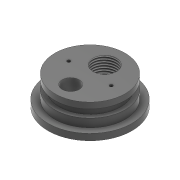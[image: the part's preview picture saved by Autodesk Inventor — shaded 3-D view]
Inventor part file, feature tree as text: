
AUTODESK INVENTOR PART (.ipt)
format: ipt  version: 2022.3 (Build 263350000, 350)  size: 176,640 bytes
history: native  units: mm
features: extrude x8, sketch x8, other x1, plane x1, thread x1
ambient origin geometry x8: Origin, YZ Plane, XZ Plane, XY Plane, X Axis, Y Axis, Z Axis, Center Point
bodies: Body1 (feature_tree)
feature tree (19):
  other  "Sólido1"
  extrude  "Extrusión1"  Depth=4.0mm TaperAngle=0.0deg
  extrude  "Extrusión2"  Depth=13.8mm TaperAngle=0.0deg
  plane  "Plano de trabajo1"
  extrude  "Extrusión6"  Depth=37.85mm
  extrude  "Extrusión7"  Depth=5.0mm
  extrude  "Extrusión8"  Depth=17.05mm
  extrude  "Extrusión9"  Depth=4.45mm
  extrude  "Extrusión10"  Depth=1.0mm
  thread  "Rosca2"  [1 undecoded]
  extrude  "Extrusión11"  Depth=5.0mm
  sketch  "Boceto1"  dims[d0=52.0mm d1=4.0mm d2=0.0mm]
  sketch  "Boceto2"  dims[d3=43.55mm d4=13.8mm d5=0.0mm]
  sketch  "Boceto6"  dims[d17=-3.6mm d18=37.85mm]
  sketch  "Boceto7"  dims[d19=5.0mm d20=0.0mm d21=5.5mm]
  sketch  "Boceto8"  dims[d22=17.05mm d23=19.15mm]
  sketch  "Boceto9"  dims[d24=4.45mm d25=0.0mm d26=10.55mm]
  sketch  "Boceto10"  dims[d27=15.0mm d28=0.0mm d29=1.0mm d30=23.25mm]
  sketch  "Boceto11"  dims[d31=4.25mm d32=0.0mm d33=14.55mm d34=4.25mm d35=0.0mm d36=13.55mm d37=0.0mm d38=13.15mm d39=13.15mm d40=2.0mm d41=2.0mm d42=5.0mm d43=0.0mm]
note: 1 required parameter value undecoded (feature->parameter linkage not recoverable at this tier; creation-order binding heuristic only, values carry confidence <= 0.55)
